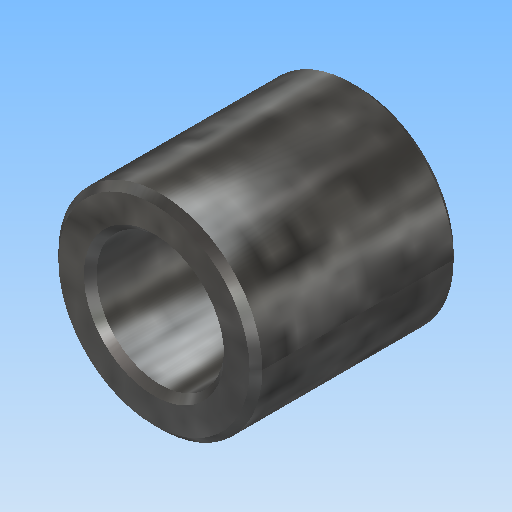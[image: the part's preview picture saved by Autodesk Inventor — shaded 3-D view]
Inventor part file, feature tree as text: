
AUTODESK INVENTOR PART (.ipt)
format: ipt  version: 2018 (Build 220112000, 112)  size: 190,976 bytes
history: native  units: mm
features: extrude x1, chamfer x1, sketch x1
ambient origin geometry x8: Origin, YZ Plane, XZ Plane, XY Plane, X Axis, Y Axis, Z Axis, Center Point
bodies: Solid1 (feature_tree)
feature tree (3):
  extrude  "Extrusion1"  Depth=16.0mm
  chamfer  "Chamfer1"  Distance=16.0mm
  sketch  "Sketch1"  dims[d0=10.0mm d1=16.0mm d2=16.0mm d3=0.0mm d4=0.5mm d5=2.0mm d6=45.0deg]
